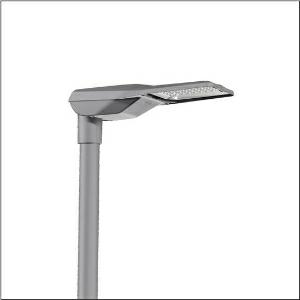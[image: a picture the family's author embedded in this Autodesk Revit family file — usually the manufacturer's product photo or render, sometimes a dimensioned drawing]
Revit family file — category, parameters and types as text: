
# Revit family: streetlight_sl_21_iq_mini___stw1_0a_5xe2e31g08jb_fb58
name_source: partatom
category: Lighting Fixtures
units: mm (PartAtom-declared; Revit-internal decimal feet)

## family parameters
Cut with Voids When Loaded = No
Host = Face
Light Source = No
Part Type = Normal
Room Calculation Point = No
Round Connector Dimension = Use Diameter
Shared = No

## types (1)
- --- (1 x LED, 10820 lm, 71.6 W, 3000K)
    Apparent Load = 72 VA
    CIE Flux Codes = 39 75 98 100 100
    Color Rendering = 70
    Color Temperature = 3000K
    Default Elevation = 1800 mm
    Description = Streetlight SL 21 iQ mini, mast luminaire, primary light control with lens, of PMMA, primary optical cover: cover, of toughened safety glass, transparent, light distribution: STW1.0a, light emission: direct distribution, primary light characteristic: asymmetric, installation type: post-top, side-entry, LED, High Power LED, rated luminous flux: 10.820lm, luminous efficacy: 151lm/W, light colour: 730, colour temperature: 3000K, control gear: iQ Street-Remote, control: Street-Remote, Auto-Match, Temp-Guard, Lumen-Switch, Night-Set, Smart-Wire, Light-Fading, Desk-Remote (wireless, voltage-free reading and setting of iQ features in the workshop via application-optimized NFC function/RFID function), optimised constant luminous flux control (CLO 2.0), pre-setting: linear dimming characteristic, mains connection: 220..240V, AC, 50/60Hz, start of lifetime: 72W, end of service life: 75W, reduction: 33W, luminaire housing, of diecast aluminium, powder-coated, SITECO metallic grey (DB 702S), corrosivity category C5 high according to DIN EN ISO 12944, please order mast flange separately, inclination adjustable: 0°, 5°, 10°, 15°, sealing non-destructively replaceable, multi-level sealing system, length: 628mm, width: 235mm, height: 110mm, mast flange for spigot size: 42mm (side-entry): 5XC10008XM4, 60/48mm (side-entry/post-top): 5XC10108XM2, 76/60mm (side-entry/post-top): 5XC10108XM1, mounting height: 4..8m, protection rating (complete): IP66, insulation class (complete): insulation class II (safety insulation), certification: CE, ENEC, ENEC+, VDE, impact resistance: IK10, permissible operating ambient temperature for outdoor applications: -40..+50°C, standard-compliant lighting for roads and squares, packaging unit: 1 piece

Light Distribution: STW1.0a
    Height = 110 mm
    Lamp = 1 x LED
    Lamp Light Flux = 10820 lm
    Lamp Power = 71.6 W
    Lamp count = 1
    Length = 625 mm
    Luminous efficacy = 151 lm/W
    Manufacturer = Siteco
    ModVariant = No
    Model = 5XE2E31G08JB
    Number of Poles = 1
    OnlyDefault = Yes
    Power Factor = 1
    Product Name = Streetlight SL 21 iQ mini | STW1.0a
    Product group = mast luminaire | pylon top
    ProductGroupID = 6100
    Protection Class = Protection class II
    Protection Degree = IP 66
    RLX_Detail_Level = 1
    RLX_Emergency_Light_Flux = 0 lm
    RLX_Emergency_Type = 0
    RLX_Emergency_Type_DB = No
    RlxData = <blob elided: 26397 chars, md5=9b2c8b91>
    Socket = socket
    Standby Power = 0 W
    System Light Flux = 10820 lm
    System Power = 72 W
    Type Comments = factory setting: luminous flux: 100 % | dim-lin: 254 | 746 mA
    Type Image = l_1003519.jpg
    URL = http://relux.com
    VarID = @adj_169673
    Voltage = 0 V
    Weight = 0.00 kg
    Width = 234 mm

## geometry (parser evidence)
native form markers: Blend x4, Sweep x12
no freeform markers — native parametric forms only
